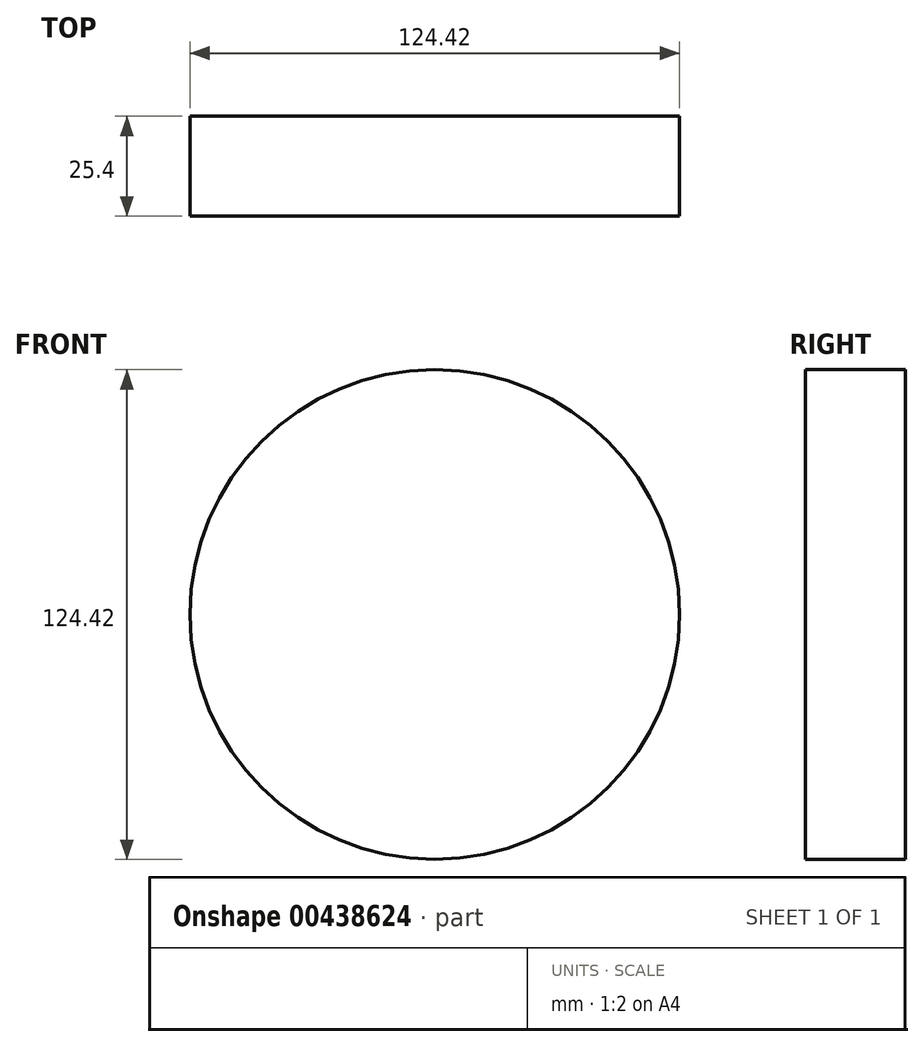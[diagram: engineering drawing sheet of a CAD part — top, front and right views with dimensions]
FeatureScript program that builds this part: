
annotation { "Feature Type Name" : "Feature", "Feature Type Description" : "" }
export const myFeature = defineFeature(function(context is Context, id is Id, definition is map)
    precondition{}
    {
        {
            var Q0;
            Q0=qCreatedBy(makeId("Front.planeOp"),FACE);
            var sketch = newSketch(context, id + "F0", { "sketchPlane" : qUnion([Q0])});
            skCircle(sketch, "E0", {"center": v(0, 0) * mm, "radius": 62.2 * mm});
            skSolve(sketch);
        }
        {
            var Q0;
            Q0=makeQuery(id+"F0.imprint","IMPRINT",FACE,{"disambiguationData":[TD([[makeQuery(id+"F0.imprint","IMPRINT",EDGE,{"derivedFrom":sQuery(id+"F0.wireOp",EDGE,"E0")}),1.0]])]});
            extrude(context, id + "F1", {"entities" : qUnion([Q0]), "depth" : 25.4 * mm});
        }
    });
